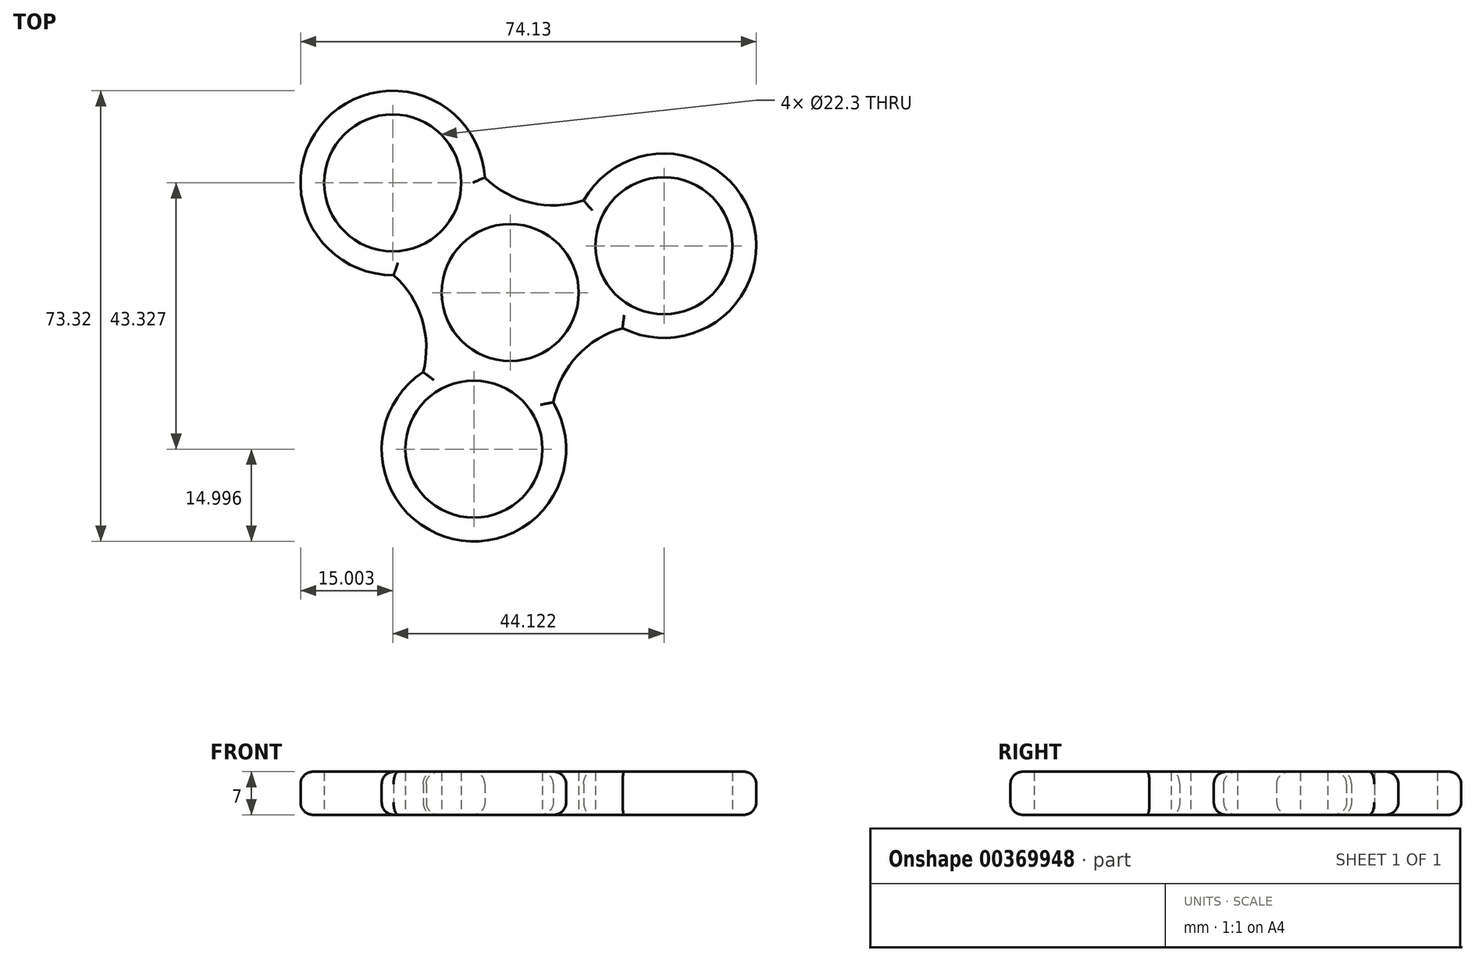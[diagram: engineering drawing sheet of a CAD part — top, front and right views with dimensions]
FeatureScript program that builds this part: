
annotation { "Feature Type Name" : "Feature", "Feature Type Description" : "" }
export const myFeature = defineFeature(function(context is Context, id is Id, definition is map)
    precondition{}
    {
        {
            var Q0;
            Q0=qCreatedBy(makeId("Top.planeOp"),FACE);
            var sketch = newSketch(context, id + "F0", { "sketchPlane" : qUnion([Q0])});
            skCircle(sketch, "E0", {"center": v(0, 0) * mm, "radius": 11.15 * mm});
            skLineSegment(sketch, "E1", {"start": v(0, 0) * mm, "end": v(-19.1, 17.85) * mm});
            skLineSegment(sketch, "E2", {"start": v(0, 0) * mm, "end": v(25.02, 7.62) * mm});
            skLineSegment(sketch, "E3", {"start": v(0, 0) * mm, "end": v(-5.9, -25.47) * mm});
            skCircle(sketch, "E4", {"center": v(-19.1, 17.85) * mm, "radius": 11.15 * mm});
            skCircle(sketch, "E5", {"center": v(25.02, 7.62) * mm, "radius": 11.15 * mm});
            skCircle(sketch, "E6", {"center": v(-5.9, -25.47) * mm, "radius": 11.15 * mm});
            skCircle(sketch, "E7", {"center": v(0, 0) * mm, "radius": 15 * mm});
            skCircle(sketch, "E8", {"center": v(-19.1, 17.85) * mm, "radius": 15 * mm});
            skCircle(sketch, "E9", {"center": v(25.02, 7.62) * mm, "radius": 15 * mm});
            skCircle(sketch, "E10", {"center": v(-5.9, -25.47) * mm, "radius": 15 * mm});
            skLineSegment(sketch, "E11", {"start": v(-19.1, 17.85) * mm, "end": v(-8.87, 28.81) * mm});
            skLineSegment(sketch, "E12", {"start": v(25.02, 7.62) * mm, "end": v(20.64, 21.97) * mm});
            skLineSegment(sketch, "E13", {"start": v(-5.9, -25.47) * mm, "end": v(8.7, -28.86) * mm});
            skLineSegment(sketch, "E14", {"start": v(-5.9, -25.47) * mm, "end": v(-20.52, -22.08) * mm});
            skLineSegment(sketch, "E15", {"start": v(-19.1, 17.85) * mm, "end": v(-29.35, 6.9) * mm});
            skLineSegment(sketch, "E16", {"start": v(25.02, 7.62) * mm, "end": v(29.39, -6.73) * mm});
            skArc(sketch, "E17", {"start": v(-8.87, 28.81) * mm, "mid": v(3.39, 14.61) * mm, "end": v(20.64, 21.97) * mm});
            skArc(sketch, "E18", {"start": v(-20.52, -22.08) * mm, "mid": v(-14.35, -4.37) * mm, "end": v(-29.35, 6.9) * mm});
            skArc(sketch, "E19", {"start": v(29.39, -6.73) * mm, "mid": v(10.96, -10.24) * mm, "end": v(8.7, -28.86) * mm});
            skSolve(sketch);
        }
        {
            var Q0;
            {var subQ0=sQuery(id+"F0.wireOp",EDGE,"E15");var subQ1=sQuery(id+"F0.wireOp",EDGE,"E4");var subQ2=makeQuery(id+"F0.imprint","INTERSECT",VERTEX,{"derivedFrom":[subQ1,subQ0]});Q0=makeQuery(id+"F0.imprint","IMPRINT",FACE,{"disambiguationData":[TD([[makeQuery(id+"F0.imprint","IMPRINT",EDGE,{"disambiguationData":[TD([[subQ2,1.0]])],"derivedFrom":subQ1}),-1.0]])]});}
            var Q1;
            {var subQ0=sQuery(id+"F0.wireOp",EDGE,"E17");var subQ2=sQuery(id+"F0.wireOp",EDGE,"E8");var subQ6=makeQuery(id+"F0.imprint","INTERSECT",VERTEX,{"derivedFrom":[subQ2,subQ0]});Q1=makeQuery(id+"F0.imprint","IMPRINT",FACE,{"disambiguationData":[TD([[makeQuery(id+"F0.imprint","IMPRINT",EDGE,{"disambiguationData":[TD([[subQ6,1.0]])],"derivedFrom":subQ2}),1.0]])]});}
            var Q2;
            {var subQ0=sQuery(id+"F0.wireOp",EDGE,"E8");var subQ3=sQuery(id+"F0.wireOp",EDGE,"E7");var subQ5=makeQuery(id+"F0.imprint","INTERSECT",VERTEX,{"disambiguationData":[OD(0.0)],"derivedFrom":[subQ3,subQ0]});Q2=makeQuery(id+"F0.imprint","IMPRINT",FACE,{"disambiguationData":[TD([[makeQuery(id+"F0.imprint","IMPRINT",EDGE,{"disambiguationData":[TD([[subQ5,-1.0]])],"derivedFrom":subQ3}),1.0]])]});}
            var Q3;
            {var subQ0=sQuery(id+"F0.wireOp",EDGE,"E8");var subQ3=sQuery(id+"F0.wireOp",EDGE,"E7");var subQ5=makeQuery(id+"F0.imprint","INTERSECT",VERTEX,{"disambiguationData":[OD(1.0)],"derivedFrom":[subQ3,subQ0]});Q3=makeQuery(id+"F0.imprint","IMPRINT",FACE,{"disambiguationData":[TD([[makeQuery(id+"F0.imprint","IMPRINT",EDGE,{"disambiguationData":[TD([[subQ5,1.0]])],"derivedFrom":subQ3}),1.0]])]});}
            var Q4;
            {var subQ0=sQuery(id+"F0.wireOp",EDGE,"E18");var subQ1=sQuery(id+"F0.wireOp",EDGE,"E8");var subQ2=makeQuery(id+"F0.imprint","INTERSECT",VERTEX,{"derivedFrom":[subQ1,subQ0]});Q4=makeQuery(id+"F0.imprint","IMPRINT",FACE,{"disambiguationData":[TD([[makeQuery(id+"F0.imprint","IMPRINT",EDGE,{"disambiguationData":[TD([[subQ2,-1.0]])],"derivedFrom":subQ1}),1.0]])]});}
            var Q5;
            {var subQ0=sQuery(id+"F0.wireOp",EDGE,"E18");var subQ2=sQuery(id+"F0.wireOp",EDGE,"E10");var subQ6=makeQuery(id+"F0.imprint","INTERSECT",VERTEX,{"derivedFrom":[subQ2,subQ0]});Q5=makeQuery(id+"F0.imprint","IMPRINT",FACE,{"disambiguationData":[TD([[makeQuery(id+"F0.imprint","IMPRINT",EDGE,{"disambiguationData":[TD([[subQ6,1.0]])],"derivedFrom":subQ2}),1.0]])]});}
            var Q6;
            {var subQ0=sQuery(id+"F0.wireOp",EDGE,"E10");var subQ3=sQuery(id+"F0.wireOp",EDGE,"E7");var subQ5=makeQuery(id+"F0.imprint","INTERSECT",VERTEX,{"disambiguationData":[OD(0.0)],"derivedFrom":[subQ3,subQ0]});Q6=makeQuery(id+"F0.imprint","IMPRINT",FACE,{"disambiguationData":[TD([[makeQuery(id+"F0.imprint","IMPRINT",EDGE,{"disambiguationData":[TD([[subQ5,-1.0]])],"derivedFrom":subQ3}),1.0]])]});}
            var Q7;
            {var subQ0=sQuery(id+"F0.wireOp",EDGE,"E10");var subQ3=sQuery(id+"F0.wireOp",EDGE,"E7");var subQ5=makeQuery(id+"F0.imprint","INTERSECT",VERTEX,{"disambiguationData":[OD(1.0)],"derivedFrom":[subQ3,subQ0]});Q7=makeQuery(id+"F0.imprint","IMPRINT",FACE,{"disambiguationData":[TD([[makeQuery(id+"F0.imprint","IMPRINT",EDGE,{"disambiguationData":[TD([[subQ5,1.0]])],"derivedFrom":subQ3}),1.0]])]});}
            var Q8;
            {var subQ0=sQuery(id+"F0.wireOp",EDGE,"E19");var subQ1=sQuery(id+"F0.wireOp",EDGE,"E10");var subQ2=makeQuery(id+"F0.imprint","INTERSECT",VERTEX,{"derivedFrom":[subQ1,subQ0]});Q8=makeQuery(id+"F0.imprint","IMPRINT",FACE,{"disambiguationData":[TD([[makeQuery(id+"F0.imprint","IMPRINT",EDGE,{"disambiguationData":[TD([[subQ2,-1.0]])],"derivedFrom":subQ1}),1.0]])]});}
            var Q9;
            {var subQ0=sQuery(id+"F0.wireOp",EDGE,"E14");var subQ1=sQuery(id+"F0.wireOp",EDGE,"E6");var subQ2=makeQuery(id+"F0.imprint","INTERSECT",VERTEX,{"derivedFrom":[subQ1,subQ0]});Q9=makeQuery(id+"F0.imprint","IMPRINT",FACE,{"disambiguationData":[TD([[makeQuery(id+"F0.imprint","IMPRINT",EDGE,{"disambiguationData":[TD([[subQ2,-1.0]])],"derivedFrom":subQ1}),-1.0]])]});}
            var Q10;
            {var subQ1=sQuery(id+"F0.wireOp",EDGE,"E7");var subQ5=makeQuery(id+"F0.imprint","INTERSECT",VERTEX,{"derivedFrom":[subQ1,sQuery(id+"F0.wireOp",EDGE,"E18")]});Q10=makeQuery(id+"F0.imprint","IMPRINT",FACE,{"disambiguationData":[TD([[makeQuery(id+"F0.imprint","IMPRINT",EDGE,{"disambiguationData":[TD([[subQ5,1.0]])],"derivedFrom":subQ1}),1.0]])]});}
            var Q11;
            {var subQ1=sQuery(id+"F0.wireOp",EDGE,"E7");var subQ5=makeQuery(id+"F0.imprint","INTERSECT",VERTEX,{"derivedFrom":[subQ1,sQuery(id+"F0.wireOp",EDGE,"E19")]});Q11=makeQuery(id+"F0.imprint","IMPRINT",FACE,{"disambiguationData":[TD([[makeQuery(id+"F0.imprint","IMPRINT",EDGE,{"disambiguationData":[TD([[subQ5,1.0]])],"derivedFrom":subQ1}),1.0]])]});}
            var Q12;
            {var subQ0=sQuery(id+"F0.wireOp",EDGE,"E9");var subQ3=sQuery(id+"F0.wireOp",EDGE,"E7");var subQ5=makeQuery(id+"F0.imprint","INTERSECT",VERTEX,{"disambiguationData":[OD(1.0)],"derivedFrom":[subQ3,subQ0]});Q12=makeQuery(id+"F0.imprint","IMPRINT",FACE,{"disambiguationData":[TD([[makeQuery(id+"F0.imprint","IMPRINT",EDGE,{"disambiguationData":[TD([[subQ5,-1.0]])],"derivedFrom":subQ3}),1.0]])]});}
            var Q13;
            {var subQ0=sQuery(id+"F0.wireOp",EDGE,"E9");var subQ3=sQuery(id+"F0.wireOp",EDGE,"E7");var subQ5=makeQuery(id+"F0.imprint","INTERSECT",VERTEX,{"disambiguationData":[OD(0.0)],"derivedFrom":[subQ3,subQ0]});Q13=makeQuery(id+"F0.imprint","IMPRINT",FACE,{"disambiguationData":[TD([[makeQuery(id+"F0.imprint","IMPRINT",EDGE,{"disambiguationData":[TD([[subQ5,1.0]])],"derivedFrom":subQ3}),1.0]])]});}
            var Q14;
            {var subQ1=sQuery(id+"F0.wireOp",EDGE,"E7");var subQ5=makeQuery(id+"F0.imprint","INTERSECT",VERTEX,{"derivedFrom":[subQ1,sQuery(id+"F0.wireOp",EDGE,"E17")]});Q14=makeQuery(id+"F0.imprint","IMPRINT",FACE,{"disambiguationData":[TD([[makeQuery(id+"F0.imprint","IMPRINT",EDGE,{"disambiguationData":[TD([[subQ5,1.0]])],"derivedFrom":subQ1}),1.0]])]});}
            var Q15;
            {var subQ0=sQuery(id+"F0.wireOp",EDGE,"E17");var subQ2=sQuery(id+"F0.wireOp",EDGE,"E9");var subQ6=makeQuery(id+"F0.imprint","INTERSECT",VERTEX,{"derivedFrom":[subQ2,subQ0]});Q15=makeQuery(id+"F0.imprint","IMPRINT",FACE,{"disambiguationData":[TD([[makeQuery(id+"F0.imprint","IMPRINT",EDGE,{"disambiguationData":[TD([[subQ6,-1.0]])],"derivedFrom":subQ2}),1.0]])]});}
            var Q16;
            {var subQ0=sQuery(id+"F0.wireOp",EDGE,"E12");var subQ1=sQuery(id+"F0.wireOp",EDGE,"E5");var subQ2=makeQuery(id+"F0.imprint","INTERSECT",VERTEX,{"derivedFrom":[subQ1,subQ0]});Q16=makeQuery(id+"F0.imprint","IMPRINT",FACE,{"disambiguationData":[TD([[makeQuery(id+"F0.imprint","IMPRINT",EDGE,{"disambiguationData":[TD([[subQ2,1.0]])],"derivedFrom":subQ1}),-1.0]])]});}
            var Q17;
            {var subQ0=sQuery(id+"F0.wireOp",EDGE,"E19");var subQ2=sQuery(id+"F0.wireOp",EDGE,"E9");var subQ9=makeQuery(id+"F0.imprint","INTERSECT",VERTEX,{"derivedFrom":[subQ2,subQ0]});Q17=makeQuery(id+"F0.imprint","IMPRINT",FACE,{"disambiguationData":[TD([[makeQuery(id+"F0.imprint","IMPRINT",EDGE,{"disambiguationData":[TD([[subQ9,1.0]])],"derivedFrom":subQ2}),1.0]])]});}
            var Q18;
            {var subQ0=sQuery(id+"F0.wireOp",EDGE,"E17");var subQ1=sQuery(id+"F0.wireOp",EDGE,"E9");var subQ3=makeQuery(id+"F0.imprint","INTERSECT",VERTEX,{"derivedFrom":[subQ1,subQ0]});Q18=makeQuery(id+"F0.imprint","IMPRINT",FACE,{"disambiguationData":[TD([[makeQuery(id+"F0.imprint","IMPRINT",EDGE,{"disambiguationData":[TD([[subQ3,1.0]])],"derivedFrom":subQ1}),1.0]])]});}
            var Q19;
            {var subQ0=sQuery(id+"F0.wireOp",EDGE,"E17");var subQ1=sQuery(id+"F0.wireOp",EDGE,"E8");var subQ3=makeQuery(id+"F0.imprint","INTERSECT",VERTEX,{"derivedFrom":[subQ1,subQ0]});Q19=makeQuery(id+"F0.imprint","IMPRINT",FACE,{"disambiguationData":[TD([[makeQuery(id+"F0.imprint","IMPRINT",EDGE,{"disambiguationData":[TD([[subQ3,-1.0]])],"derivedFrom":subQ1}),1.0]])]});}
            var Q20;
            {var subQ0=sQuery(id+"F0.wireOp",EDGE,"E18");var subQ1=sQuery(id+"F0.wireOp",EDGE,"E8");var subQ3=makeQuery(id+"F0.imprint","INTERSECT",VERTEX,{"derivedFrom":[subQ1,subQ0]});Q20=makeQuery(id+"F0.imprint","IMPRINT",FACE,{"disambiguationData":[TD([[makeQuery(id+"F0.imprint","IMPRINT",EDGE,{"disambiguationData":[TD([[subQ3,1.0]])],"derivedFrom":subQ1}),1.0]])]});}
            var Q21;
            {var subQ0=sQuery(id+"F0.wireOp",EDGE,"E18");var subQ1=sQuery(id+"F0.wireOp",EDGE,"E10");var subQ3=makeQuery(id+"F0.imprint","INTERSECT",VERTEX,{"derivedFrom":[subQ1,subQ0]});Q21=makeQuery(id+"F0.imprint","IMPRINT",FACE,{"disambiguationData":[TD([[makeQuery(id+"F0.imprint","IMPRINT",EDGE,{"disambiguationData":[TD([[subQ3,-1.0]])],"derivedFrom":subQ1}),1.0]])]});}
            var Q22;
            {var subQ0=sQuery(id+"F0.wireOp",EDGE,"E19");var subQ1=sQuery(id+"F0.wireOp",EDGE,"E9");var subQ3=makeQuery(id+"F0.imprint","INTERSECT",VERTEX,{"derivedFrom":[subQ1,subQ0]});Q22=makeQuery(id+"F0.imprint","IMPRINT",FACE,{"disambiguationData":[TD([[makeQuery(id+"F0.imprint","IMPRINT",EDGE,{"disambiguationData":[TD([[subQ3,-1.0]])],"derivedFrom":subQ1}),1.0]])]});}
            var Q23;
            {var subQ0=sQuery(id+"F0.wireOp",EDGE,"E19");var subQ1=sQuery(id+"F0.wireOp",EDGE,"E10");var subQ3=makeQuery(id+"F0.imprint","INTERSECT",VERTEX,{"derivedFrom":[subQ1,subQ0]});Q23=makeQuery(id+"F0.imprint","IMPRINT",FACE,{"disambiguationData":[TD([[makeQuery(id+"F0.imprint","IMPRINT",EDGE,{"disambiguationData":[TD([[subQ3,1.0]])],"derivedFrom":subQ1}),1.0]])]});}
            var Q24;
            {var subQ0=sQuery(id+"F0.wireOp",EDGE,"E18");var subQ1=sQuery(id+"F0.wireOp",EDGE,"E7");var subQ2=makeQuery(id+"F0.imprint","INTERSECT",VERTEX,{"derivedFrom":[subQ1,subQ0]});Q24=makeQuery(id+"F0.imprint","IMPRINT",FACE,{"disambiguationData":[TD([[makeQuery(id+"F0.imprint","IMPRINT",EDGE,{"disambiguationData":[TD([[subQ2,-1.0]])],"derivedFrom":subQ1}),-1.0]])]});}
            var Q25;
            {var subQ0=sQuery(id+"F0.wireOp",EDGE,"E18");var subQ1=sQuery(id+"F0.wireOp",EDGE,"E7");var subQ2=makeQuery(id+"F0.imprint","INTERSECT",VERTEX,{"derivedFrom":[subQ1,subQ0]});Q25=makeQuery(id+"F0.imprint","IMPRINT",FACE,{"disambiguationData":[TD([[makeQuery(id+"F0.imprint","IMPRINT",EDGE,{"disambiguationData":[TD([[subQ2,1.0]])],"derivedFrom":subQ1}),-1.0]])]});}
            var Q26;
            {var subQ0=sQuery(id+"F0.wireOp",EDGE,"E17");var subQ1=sQuery(id+"F0.wireOp",EDGE,"E7");var subQ2=makeQuery(id+"F0.imprint","INTERSECT",VERTEX,{"derivedFrom":[subQ1,subQ0]});Q26=makeQuery(id+"F0.imprint","IMPRINT",FACE,{"disambiguationData":[TD([[makeQuery(id+"F0.imprint","IMPRINT",EDGE,{"disambiguationData":[TD([[subQ2,-1.0]])],"derivedFrom":subQ1}),-1.0]])]});}
            var Q27;
            {var subQ0=sQuery(id+"F0.wireOp",EDGE,"E17");var subQ1=sQuery(id+"F0.wireOp",EDGE,"E7");var subQ2=makeQuery(id+"F0.imprint","INTERSECT",VERTEX,{"derivedFrom":[subQ1,subQ0]});Q27=makeQuery(id+"F0.imprint","IMPRINT",FACE,{"disambiguationData":[TD([[makeQuery(id+"F0.imprint","IMPRINT",EDGE,{"disambiguationData":[TD([[subQ2,1.0]])],"derivedFrom":subQ1}),-1.0]])]});}
            var Q28;
            {var subQ0=sQuery(id+"F0.wireOp",EDGE,"E19");var subQ1=sQuery(id+"F0.wireOp",EDGE,"E7");var subQ2=makeQuery(id+"F0.imprint","INTERSECT",VERTEX,{"derivedFrom":[subQ1,subQ0]});Q28=makeQuery(id+"F0.imprint","IMPRINT",FACE,{"disambiguationData":[TD([[makeQuery(id+"F0.imprint","IMPRINT",EDGE,{"disambiguationData":[TD([[subQ2,-1.0]])],"derivedFrom":subQ1}),-1.0]])]});}
            var Q29;
            {var subQ0=sQuery(id+"F0.wireOp",EDGE,"E19");var subQ1=sQuery(id+"F0.wireOp",EDGE,"E7");var subQ2=makeQuery(id+"F0.imprint","INTERSECT",VERTEX,{"derivedFrom":[subQ1,subQ0]});Q29=makeQuery(id+"F0.imprint","IMPRINT",FACE,{"disambiguationData":[TD([[makeQuery(id+"F0.imprint","IMPRINT",EDGE,{"disambiguationData":[TD([[subQ2,1.0]])],"derivedFrom":subQ1}),-1.0]])]});}
            extrude(context, id + "F1", {"entities" : qUnion([Q0, Q1, Q2, Q3, Q4, Q5, Q6, Q7, Q8, Q9, Q10, Q11, Q12, Q13, Q14, Q15, Q16, Q17, Q18, Q19, Q20, Q21, Q22, Q23, Q24, Q25, Q26, Q27, Q28, Q29]), "depth" : 7 * mm, "offsetDistance" : 25 * mm});
        }
        {
            var Q0;
            Q0=makeQuery(id+"F1.opExtrude","CAP_EDGE",EDGE,{"disambiguationData":[OSD([sQuery(id+"F0.wireOp",EDGE,"E17")])],"isStart":false});
            var Q1;
            Q1=makeQuery(id+"F1.opExtrude","CAP_EDGE",EDGE,{"disambiguationData":[OSD([sQuery(id+"F0.wireOp",EDGE,"E8")])],"isStart":false});
            var Q2;
            Q2=makeQuery(id+"F1.opExtrude","CAP_EDGE",EDGE,{"disambiguationData":[OSD([sQuery(id+"F0.wireOp",EDGE,"E9")])],"isStart":false});
            var Q3;
            Q3=makeQuery(id+"F1.opExtrude","CAP_EDGE",EDGE,{"disambiguationData":[OSD([sQuery(id+"F0.wireOp",EDGE,"E19")])],"isStart":false});
            var Q4;
            Q4=makeQuery(id+"F1.opExtrude","CAP_EDGE",EDGE,{"disambiguationData":[OSD([sQuery(id+"F0.wireOp",EDGE,"E18")])],"isStart":false});
            var Q5;
            Q5=makeQuery(id+"F1.opExtrude","CAP_EDGE",EDGE,{"disambiguationData":[OSD([sQuery(id+"F0.wireOp",EDGE,"E10")])],"isStart":false});
            var Q6;
            Q6=makeQuery(id+"F1.opExtrude","CAP_EDGE",EDGE,{"disambiguationData":[OSD([sQuery(id+"F0.wireOp",EDGE,"E17")])],"isStart":true});
            var Q7;
            Q7=makeQuery(id+"F1.opExtrude","CAP_EDGE",EDGE,{"disambiguationData":[OSD([sQuery(id+"F0.wireOp",EDGE,"E8")])],"isStart":true});
            var Q8;
            Q8=makeQuery(id+"F1.opExtrude","CAP_EDGE",EDGE,{"disambiguationData":[OSD([sQuery(id+"F0.wireOp",EDGE,"E9")])],"isStart":true});
            var Q9;
            Q9=makeQuery(id+"F1.opExtrude","CAP_EDGE",EDGE,{"disambiguationData":[OSD([sQuery(id+"F0.wireOp",EDGE,"E19")])],"isStart":true});
            var Q10;
            Q10=makeQuery(id+"F1.opExtrude","CAP_EDGE",EDGE,{"disambiguationData":[OSD([sQuery(id+"F0.wireOp",EDGE,"E18")])],"isStart":true});
            var Q11;
            Q11=makeQuery(id+"F1.opExtrude","CAP_EDGE",EDGE,{"disambiguationData":[OSD([sQuery(id+"F0.wireOp",EDGE,"E10")])],"isStart":true});
            fillet(context, id + "F2", {"entities" : qUnion([Q0, Q1, Q2, Q3, Q4, Q5, Q6, Q7, Q8, Q9, Q10, Q11]), "radius" : 2 * mm, "tangentPropagation" : true, "allowEdgeOverflow" : false});
        }
    });
